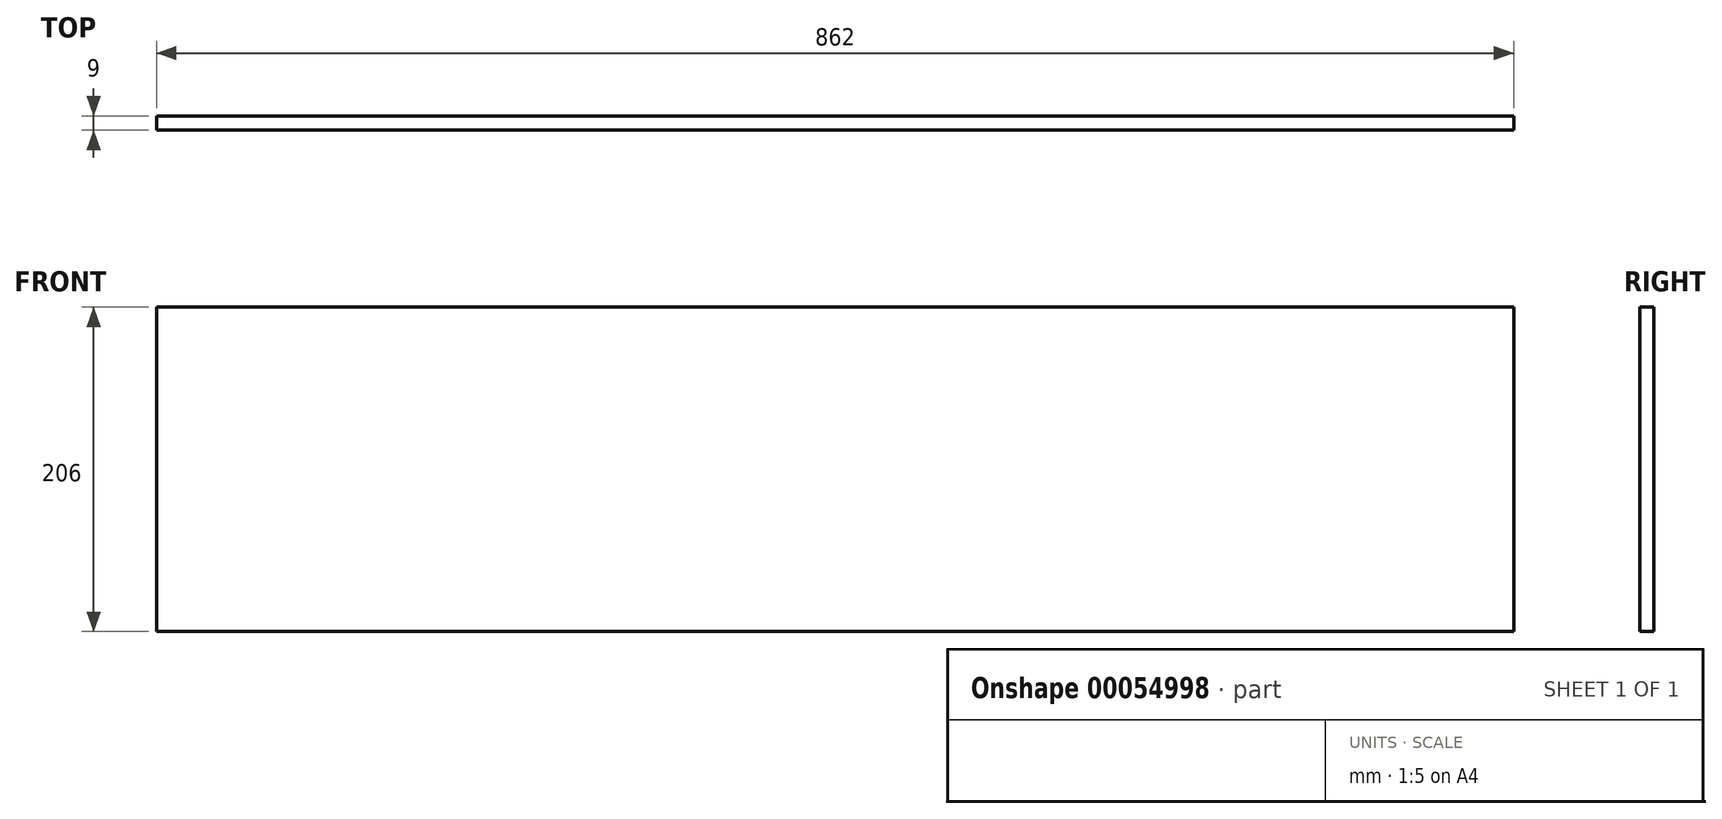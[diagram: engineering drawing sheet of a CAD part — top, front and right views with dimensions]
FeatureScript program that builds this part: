
annotation { "Feature Type Name" : "Feature", "Feature Type Description" : "" }
export const myFeature = defineFeature(function(context is Context, id is Id, definition is map)
    precondition{}
    {
        {
            var Q0;
            Q0=qCreatedBy(makeId("Front.planeOp"),FACE);
            var sketch = newSketch(context, id + "F0", { "sketchPlane" : qUnion([Q0])});
            skLineSegment(sketch, "E0.bottom", {"start": v(-426.22, 7.3) * mm, "end": v(435.78, 7.3) * mm});
            skLineSegment(sketch, "E0.top", {"start": v(-426.22, -198.7) * mm, "end": v(435.78, -198.7) * mm});
            skLineSegment(sketch, "E0.left", {"start": v(-426.22, 7.3) * mm, "end": v(-426.22, -198.7) * mm});
            skLineSegment(sketch, "E0.right", {"start": v(435.78, 7.3) * mm, "end": v(435.78, -198.7) * mm});
            skSolve(sketch);
        }
        {
            var Q0;
            Q0 = qSketchRegion(id + "F0", true);
            extrude(context, id + "F1", {"entities" : qUnion([Q0]), "depth" : 9 * mm});
        }
    });
